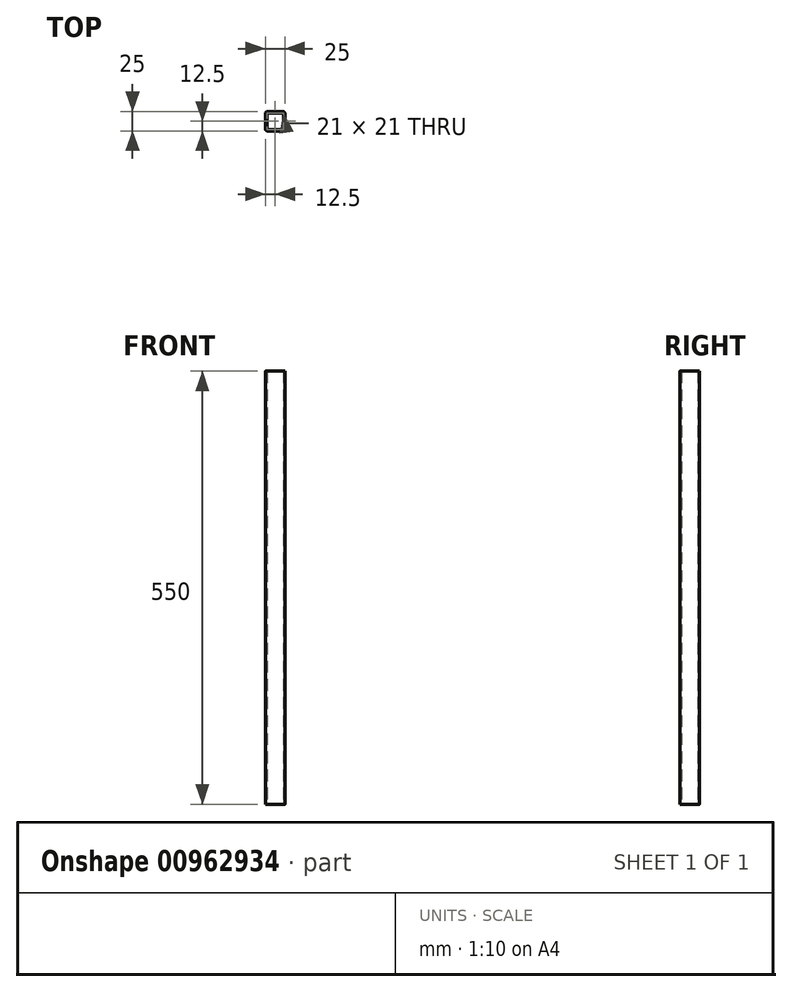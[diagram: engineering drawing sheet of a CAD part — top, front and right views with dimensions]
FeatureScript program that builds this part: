
annotation { "Feature Type Name" : "Feature", "Feature Type Description" : "" }
export const myFeature = defineFeature(function(context is Context, id is Id, definition is map)
    precondition{}
    {
        {
            var Q0;
            Q0=qCreatedBy(makeId("Top.planeOp"),FACE);
            var sketch = newSketch(context, id + "F0", { "sketchPlane" : qUnion([Q0])});
            skLineSegment(sketch, "E0.bottom", {"start": v(9.5, 12.5) * mm, "end": v(-9.5, 12.5) * mm});
            skLineSegment(sketch, "E0.top", {"start": v(9.5, -12.5) * mm, "end": v(-9.5, -12.5) * mm});
            skLineSegment(sketch, "E0.left", {"start": v(12.5, 9.5) * mm, "end": v(12.5, -9.5) * mm});
            skLineSegment(sketch, "E0.right", {"start": v(-12.5, 9.5) * mm, "end": v(-12.5, -9.5) * mm});
            skPoint(sketch, "E0.middle", {"position": v(0, 0) * mm});
            skPoint(sketch, "E1.visualSharp", {"position": v(-12.5, 12.5) * mm});
            skArc(sketch, "E1.filletArc", {"start": v(-9.5, 12.5) * mm, "mid": v(-11.62, 11.62) * mm, "end": v(-12.5, 9.5) * mm});
            skPoint(sketch, "E2.visualSharp", {"position": v(-12.5, -12.5) * mm});
            skArc(sketch, "E2.filletArc", {"start": v(-12.5, -9.5) * mm, "mid": v(-11.62, -11.62) * mm, "end": v(-9.5, -12.5) * mm});
            skPoint(sketch, "E3.visualSharp", {"position": v(12.5, -12.5) * mm});
            skArc(sketch, "E3.filletArc", {"start": v(9.5, -12.5) * mm, "mid": v(11.62, -11.62) * mm, "end": v(12.5, -9.5) * mm});
            skPoint(sketch, "E4.visualSharp", {"position": v(12.5, 12.5) * mm});
            skArc(sketch, "E4.filletArc", {"start": v(12.5, 9.5) * mm, "mid": v(11.62, 11.62) * mm, "end": v(9.5, 12.5) * mm});
            skLineSegment(sketch, "E5.0", {"start": v(10.5, 10.5) * mm, "end": v(-10.5, 10.5) * mm});
            skLineSegment(sketch, "E5.1", {"start": v(10.5, 10.5) * mm, "end": v(10.5, -10.5) * mm});
            skLineSegment(sketch, "E5.2", {"start": v(10.5, -10.5) * mm, "end": v(-10.5, -10.5) * mm});
            skLineSegment(sketch, "E5.3", {"start": v(-10.5, 10.5) * mm, "end": v(-10.5, -10.5) * mm});
            skSolve(sketch);
        }
        {
            var Q0;
            Q0=makeQuery(id+"F0.imprint","IMPRINT",FACE,{"disambiguationData":[TD([[makeQuery(id+"F0.imprint","IMPRINT",EDGE,{"derivedFrom":sQuery(id+"F0.wireOp",EDGE,"E0.bottom")}),1.0]])]});
            extrude(context, id + "F1", {"entities" : qUnion([Q0]), "depth" : 550 * mm, "offsetDistance" : 25 * mm});
        }
    });
